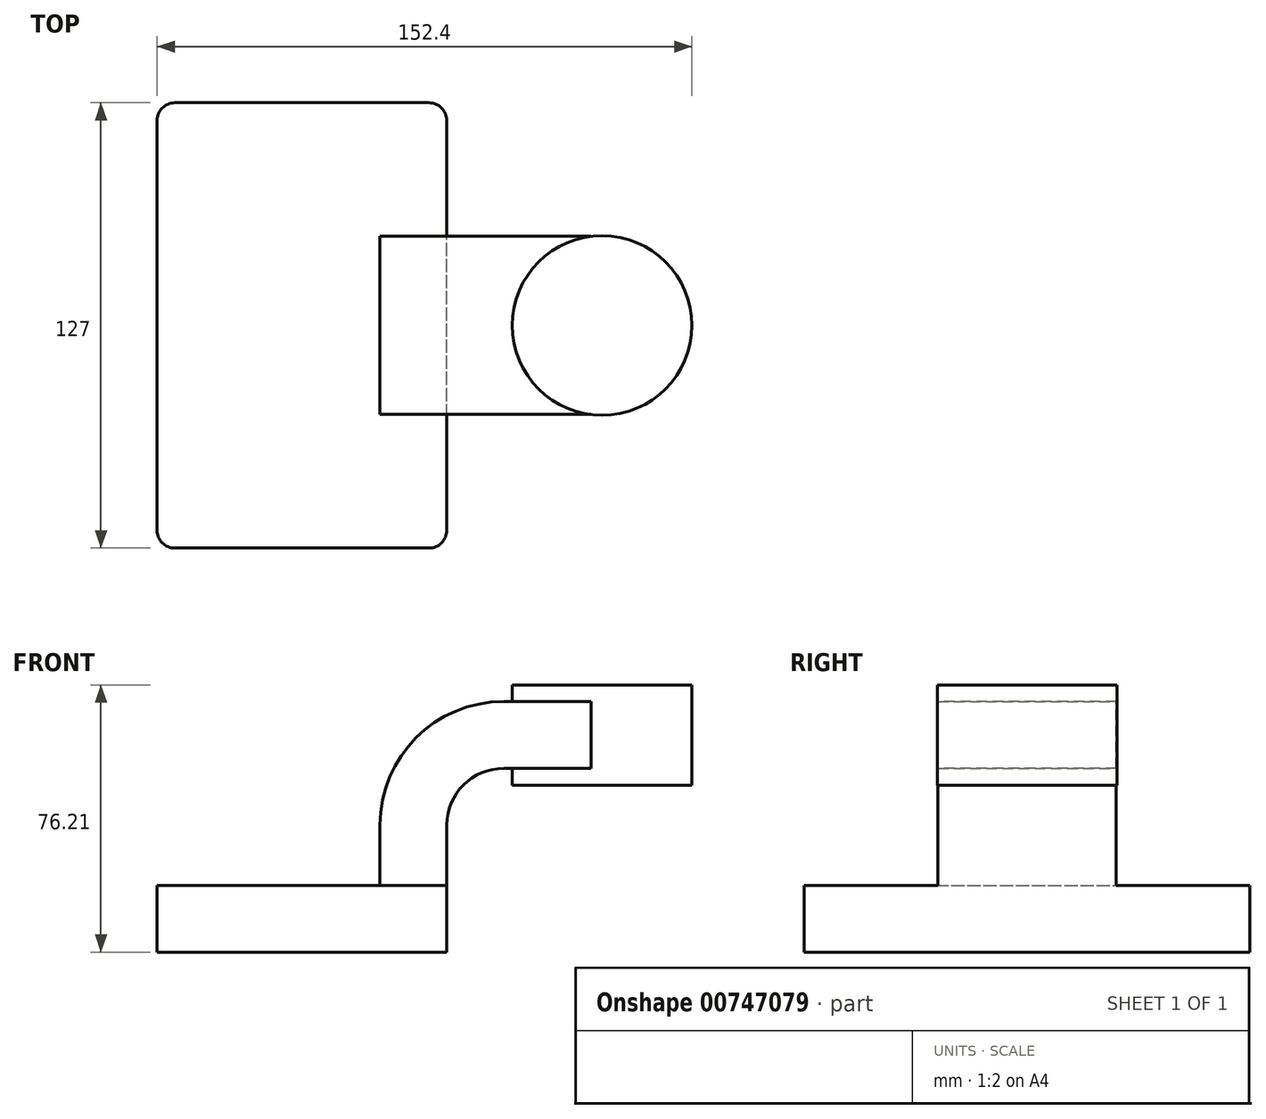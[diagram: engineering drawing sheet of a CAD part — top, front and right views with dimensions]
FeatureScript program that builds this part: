
annotation { "Feature Type Name" : "Feature", "Feature Type Description" : "" }
export const myFeature = defineFeature(function(context is Context, id is Id, definition is map)
    precondition{}
    {
        {
            var Q0;
            Q0=qCreatedBy(makeId("Front.planeOp"),FACE);
            var sketch = newSketch(context, id + "F0", { "sketchPlane" : qUnion([Q0])});
            skLineSegment(sketch, "E0.bottom", {"start": v(41.28, -9.52) * mm, "end": v(-41.28, -9.53) * mm});
            skLineSegment(sketch, "E0.top", {"start": v(41.28, 9.53) * mm, "end": v(-41.28, 9.53) * mm});
            skLineSegment(sketch, "E0.left", {"start": v(41.28, -9.52) * mm, "end": v(41.28, 9.53) * mm});
            skLineSegment(sketch, "E0.right", {"start": v(-41.28, -9.53) * mm, "end": v(-41.28, 9.53) * mm});
            skPoint(sketch, "E0.middle", {"position": v(0, 0) * mm});
            skLineSegment(sketch, "E1.bottom", {"start": v(60.33, 38.1) * mm, "end": v(111.12, 38.1) * mm});
            skLineSegment(sketch, "E1.top", {"start": v(60.33, 66.68) * mm, "end": v(111.12, 66.68) * mm});
            skLineSegment(sketch, "E1.left", {"start": v(60.33, 38.1) * mm, "end": v(60.33, 66.68) * mm});
            skLineSegment(sketch, "E1.right", {"start": v(111.12, 38.1) * mm, "end": v(111.12, 66.68) * mm});
            skPoint(sketch, "E1.middle", {"position": v(85.72, 52.39) * mm});
            skLineSegment(sketch, "E2", {"start": v(41.28, 9.53) * mm, "end": v(41.28, 26.7) * mm});
            skArc(sketch, "E3", {"start": v(41.28, 26.7) * mm, "mid": v(46.01, 38.14) * mm, "end": v(57.45, 42.88) * mm});
            skLineSegment(sketch, "E4", {"start": v(57.45, 42.88) * mm, "end": v(85.53, 42.88) * mm});
            skLineSegment(sketch, "E5.0", {"start": v(57.45, 61.93) * mm, "end": v(85.53, 61.93) * mm});
            skArc(sketch, "E5.1", {"start": v(22.23, 26.7) * mm, "mid": v(32.54, 51.6) * mm, "end": v(57.45, 61.93) * mm});
            skLineSegment(sketch, "E5.2", {"start": v(22.22, 9.53) * mm, "end": v(22.22, 26.7) * mm});
            skFitSpline(sketch, "E6", {"points": [v(-41.28, 9.52) * mm, v(57.45, 61.93) * mm], "startDerivative": vector(2.3, 131.25) * mm, "endDerivative": vector(141.12, -8) * mm});
            skLineSegment(sketch, "E7", {"start": v(85.53, 66.68) * mm, "end": v(85.53, 38.1) * mm});
            skPoint(sketch, "E7.endSnap0", {"position": v(85.72, 38.1) * mm});
            skSolve(sketch);
        }
        {
            var Q0;
            Q0=makeQuery(id+"F0.imprint","IMPRINT",FACE,{"disambiguationData":[TD([[makeQuery(id+"F0.imprint","IMPRINT",EDGE,{"derivedFrom":sQuery(id+"F0.wireOp",EDGE,"E0.bottom")}),-1.0]])]});
            extrude(context, id + "F1", {"entities" : qUnion([Q0]), "endBound" : BoundingType.SYMMETRIC, "depth" : 127 * mm, "offsetDistance" : 25.4 * mm});
        }
        {
            var Q0;
            {var subQ1=sQuery(id+"F0.wireOp",EDGE,"E2");Q0=makeQuery(id+"F0.imprint","IMPRINT",FACE,{"disambiguationData":[TD([[makeQuery(id+"F0.imprint","IMPRINT",EDGE,{"derivedFrom":subQ1}),1.0]])]});}
            var Q1;
            {var subQ5=sQuery(id+"F0.wireOp",EDGE,"aj4RjpZ6-6YBT-OFYV-Wsim-T1akdPxrT28U");Q1=makeQuery(id+"F0.imprint","IMPRINT",FACE,{"disambiguationData":[TD([[makeQuery(id+"F0.imprint","IMPRINT",EDGE,{"derivedFrom":subQ5}),-1.0]])]});}
            extrude(context, id + "F2", {"entities" : qUnion([Q0, Q1]), "operationType" : NewBodyOperationType.ADD, "endBound" : BoundingType.SYMMETRIC, "depth" : 50.8 * mm, "offsetDistance" : 25.4 * mm});
        }
        {
            var Q0;
            Q0=makeQuery(id+"F0.imprint","IMPRINT",FACE,{"disambiguationData":[TD([[makeQuery(id+"F0.imprint","IMPRINT",EDGE,{"derivedFrom":sQuery(id+"F0.wireOp",EDGE,"E5.1")}),1.0]])]});
            extrude(context, id + "F3", {"entities" : qUnion([Q0]), "operationType" : NewBodyOperationType.ADD, "endBound" : BoundingType.SYMMETRIC, "depth" : 6.73 * mm, "offsetDistance" : 25.4 * mm});
        }
        {
            var Q0;
            {var subQ0=sQuery(id+"F0.wireOp",EDGE,"E4");var subQ1=sQuery(id+"F0.wireOp",EDGE,"E1.left");var subQ2=makeQuery(id+"F0.imprint","INTERSECT",VERTEX,{"derivedFrom":[subQ1,subQ0]});Q0=makeQuery(id+"F0.imprint","IMPRINT",FACE,{"disambiguationData":[TD([[makeQuery(id+"F0.imprint","IMPRINT",EDGE,{"disambiguationData":[TD([[subQ2,-1.0]])],"derivedFrom":subQ1}),-1.0]])]});}
            extrude(context, id + "F4", {"entities" : qUnion([Q0]), "operationType" : NewBodyOperationType.ADD, "endBound" : BoundingType.SYMMETRIC, "depth" : 50.8 * mm, "offsetDistance" : 25.4 * mm});
        }
        {
            var Q0;
            {var subQ4=sQuery(id+"F0.wireOp",EDGE,"E1.right");Q0=makeQuery(id+"F0.imprint","IMPRINT",FACE,{"disambiguationData":[TD([[makeQuery(id+"F0.imprint","IMPRINT",EDGE,{"derivedFrom":subQ4}),1.0]])]});}
            var Q1;
            Q1=sQuery(id+"F0.wireOp",EDGE,"E7");
            revolve(context, id + "F5", {"operationType" : NewBodyOperationType.ADD, "surfaceOperationType" : NewSurfaceOperationType.NEW, "entities" : qUnion([Q0]), "axis" : qUnion([Q1]), "revolveType" : RevolveType.FULL});
        }
        {
            var Q0;
            Q0=makeQuery(id+"F1.opExtrude","CAP_EDGE",EDGE,{"disambiguationData":[OSD([sQuery(id+"F0.wireOp",EDGE,"E0.left")])],"isStart":false});
            var Q1;
            Q1=makeQuery(id+"F1.opExtrude","CAP_EDGE",EDGE,{"disambiguationData":[OSD([sQuery(id+"F0.wireOp",EDGE,"E0.right")])],"isStart":false});
            var Q2;
            Q2=makeQuery(id+"F1.opExtrude","CAP_EDGE",EDGE,{"disambiguationData":[OSD([sQuery(id+"F0.wireOp",EDGE,"E0.left")])],"isStart":true});
            var Q3;
            Q3=makeQuery(id+"F1.opExtrude","CAP_EDGE",EDGE,{"disambiguationData":[OSD([sQuery(id+"F0.wireOp",EDGE,"E0.right")])],"isStart":true});
            fillet(context, id + "F6", {"entities" : qUnion([Q0, Q1, Q2, Q3]), "radius" : 5.08 * mm, "tangentPropagation" : true, "allowEdgeOverflow" : false});
        }
    });
